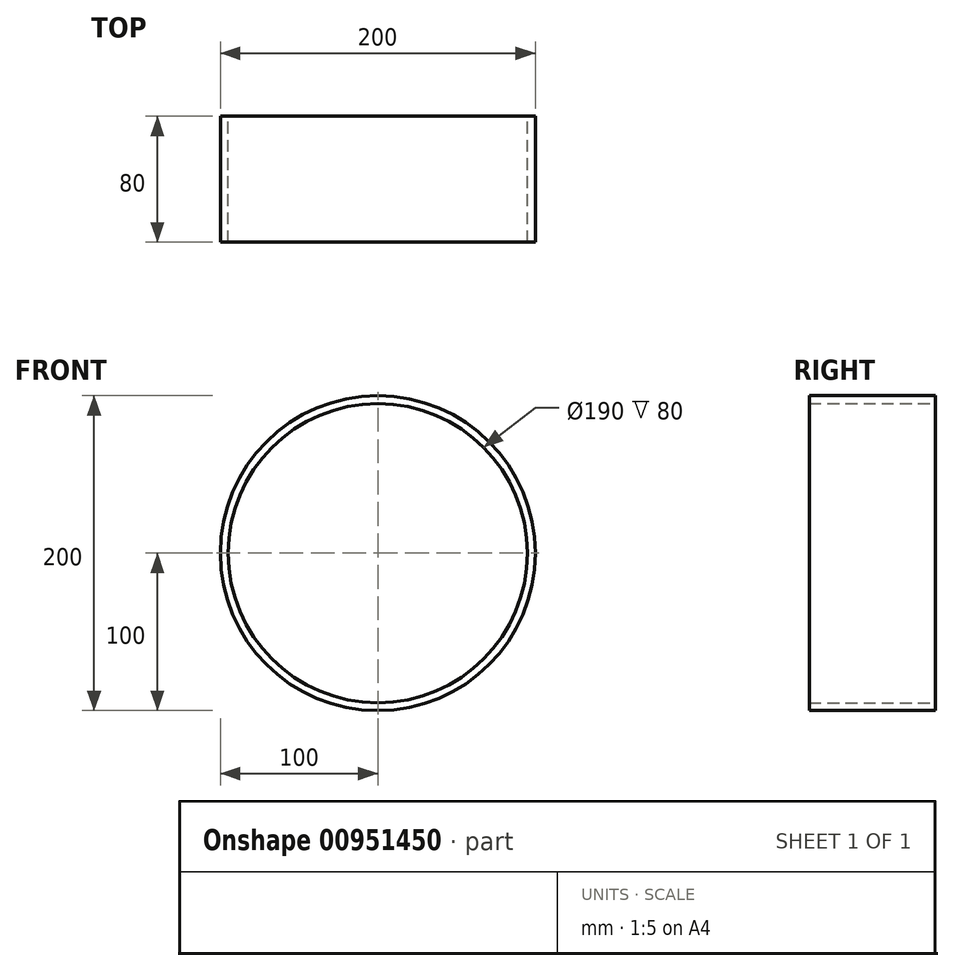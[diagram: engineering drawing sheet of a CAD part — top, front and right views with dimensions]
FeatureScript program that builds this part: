
annotation { "Feature Type Name" : "Feature", "Feature Type Description" : "" }
export const myFeature = defineFeature(function(context is Context, id is Id, definition is map)
    precondition{}
    {
        {
            var Q0;
            Q0=qCreatedBy(makeId("Front.planeOp"),FACE);
            var sketch = newSketch(context, id + "F0", { "sketchPlane" : qUnion([Q0])});
            skCircle(sketch, "E0", {"center": v(0, 0) * mm, "radius": 100 * mm});
            skCircle(sketch, "E1", {"center": v(0, 0) * mm, "radius": 95 * mm});
            skSolve(sketch);
        }
        {
            var Q0;
            Q0=makeQuery(id+"F0.imprint","IMPRINT",FACE,{"disambiguationData":[TD([[makeQuery(id+"F0.imprint","IMPRINT",EDGE,{"derivedFrom":sQuery(id+"F0.wireOp",EDGE,"E0")}),1.0]])]});
            extrude(context, id + "F1", {"entities" : qUnion([Q0]), "depth" : 80 * mm, "offsetDistance" : 25 * mm});
        }
    });
